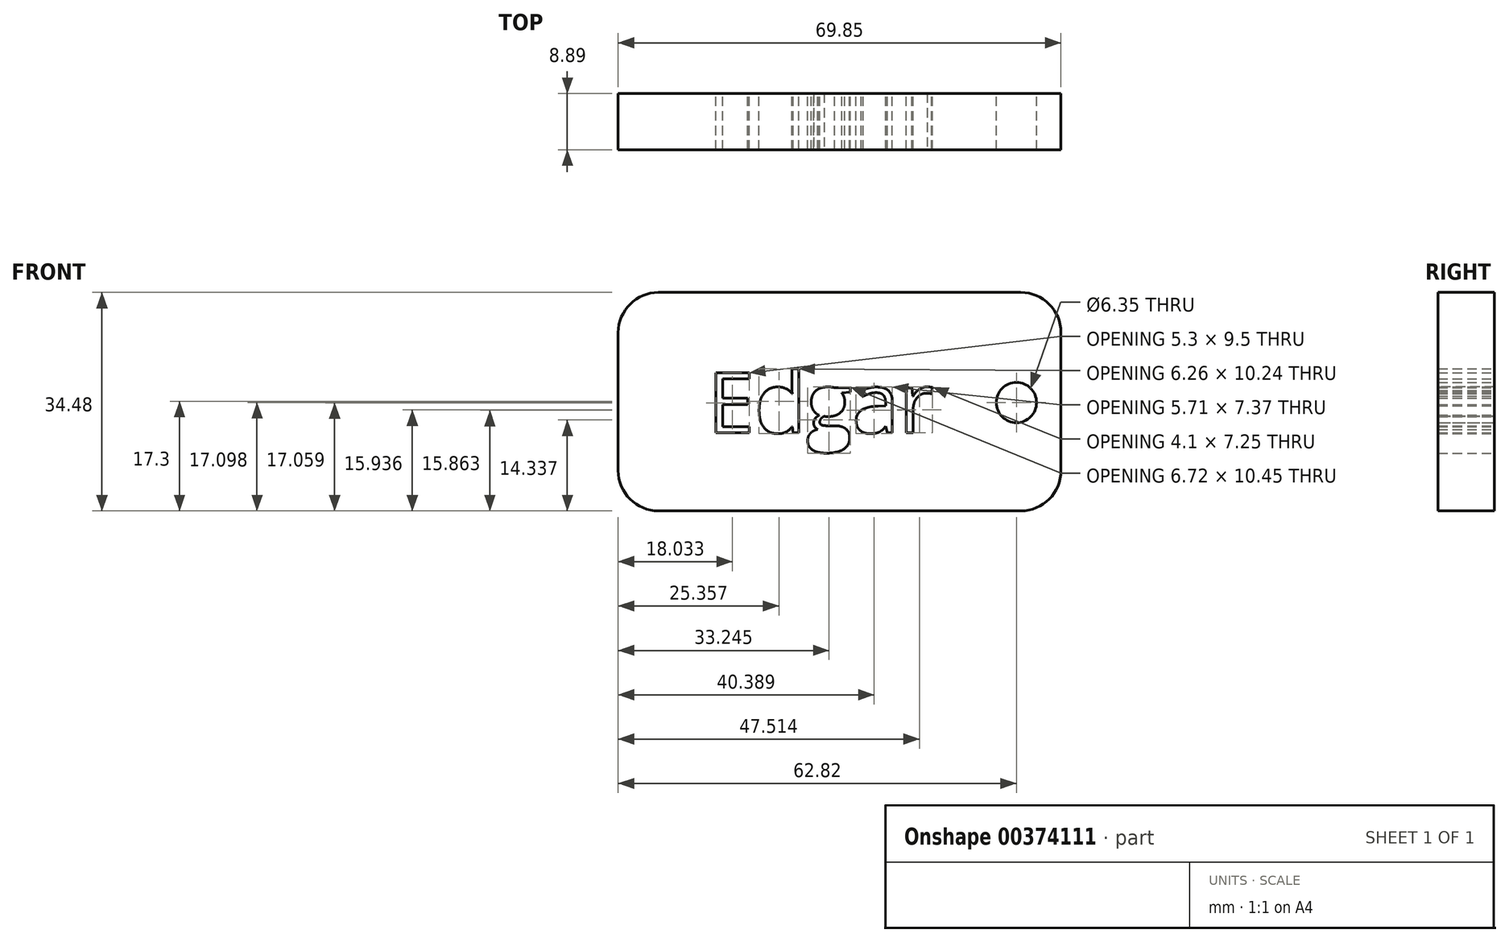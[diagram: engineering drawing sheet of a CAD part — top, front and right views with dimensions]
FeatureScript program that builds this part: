
annotation { "Feature Type Name" : "Feature", "Feature Type Description" : "" }
export const myFeature = defineFeature(function(context is Context, id is Id, definition is map)
    precondition{}
    {
        {
            var Q0;
            Q0=qCreatedBy(makeId("Front.planeOp"),FACE);
            var sketch = newSketch(context, id + "F0", { "sketchPlane" : qUnion([Q0])});
            skLineSegment(sketch, "E0.bottom", {"start": v(-15.62, -12.6) * mm, "end": v(41.53, -12.6) * mm});
            skLineSegment(sketch, "E0.top", {"start": v(-15.62, 21.89) * mm, "end": v(41.53, 21.89) * mm});
            skLineSegment(sketch, "E0.left", {"start": v(-21.97, -6.24) * mm, "end": v(-21.97, 15.54) * mm});
            skLineSegment(sketch, "E0.right", {"start": v(47.88, -6.24) * mm, "end": v(47.88, 15.54) * mm});
            skPoint(sketch, "E1.visualSharp", {"position": v(-21.97, 21.89) * mm});
            skArc(sketch, "E1.filletArc", {"start": v(-15.62, 21.89) * mm, "mid": v(-20.1, 20.03) * mm, "end": v(-21.97, 15.54) * mm});
            skPoint(sketch, "E2.visualSharp", {"position": v(47.88, 21.89) * mm});
            skArc(sketch, "E2.filletArc", {"start": v(47.88, 15.54) * mm, "mid": v(46.02, 20.03) * mm, "end": v(41.53, 21.89) * mm});
            skPoint(sketch, "E3.visualSharp", {"position": v(47.88, -12.6) * mm});
            skArc(sketch, "E3.filletArc", {"start": v(41.53, -12.6) * mm, "mid": v(46.02, -10.73) * mm, "end": v(47.88, -6.24) * mm});
            skPoint(sketch, "E4.visualSharp", {"position": v(-21.97, -12.6) * mm});
            skArc(sketch, "E4.filletArc", {"start": v(-21.97, -6.24) * mm, "mid": v(-20.1, -10.73) * mm, "end": v(-15.62, -12.6) * mm});
            skCircle(sketch, "E5", {"center": v(40.85, 4.5) * mm, "radius": 3.18 * mm});
            skText(sketch, "E6", { "text": "Edgar", "fontName": "OpenSans-Regular.ttf"});
            const initialGuessF0  = {"E6": [-0.00789, -0.00028, 1, 0, 0.00958]};
            skSetInitialGuess(sketch, initialGuessF0);
            skSolve(sketch);
        }
        {
            var Q0;
            Q0 = qSketchRegion(id + "F0", true);
            extrude(context, id + "F1", {"entities" : qUnion([Q0]), "depth" : 8.9 * mm});
        }
    });
